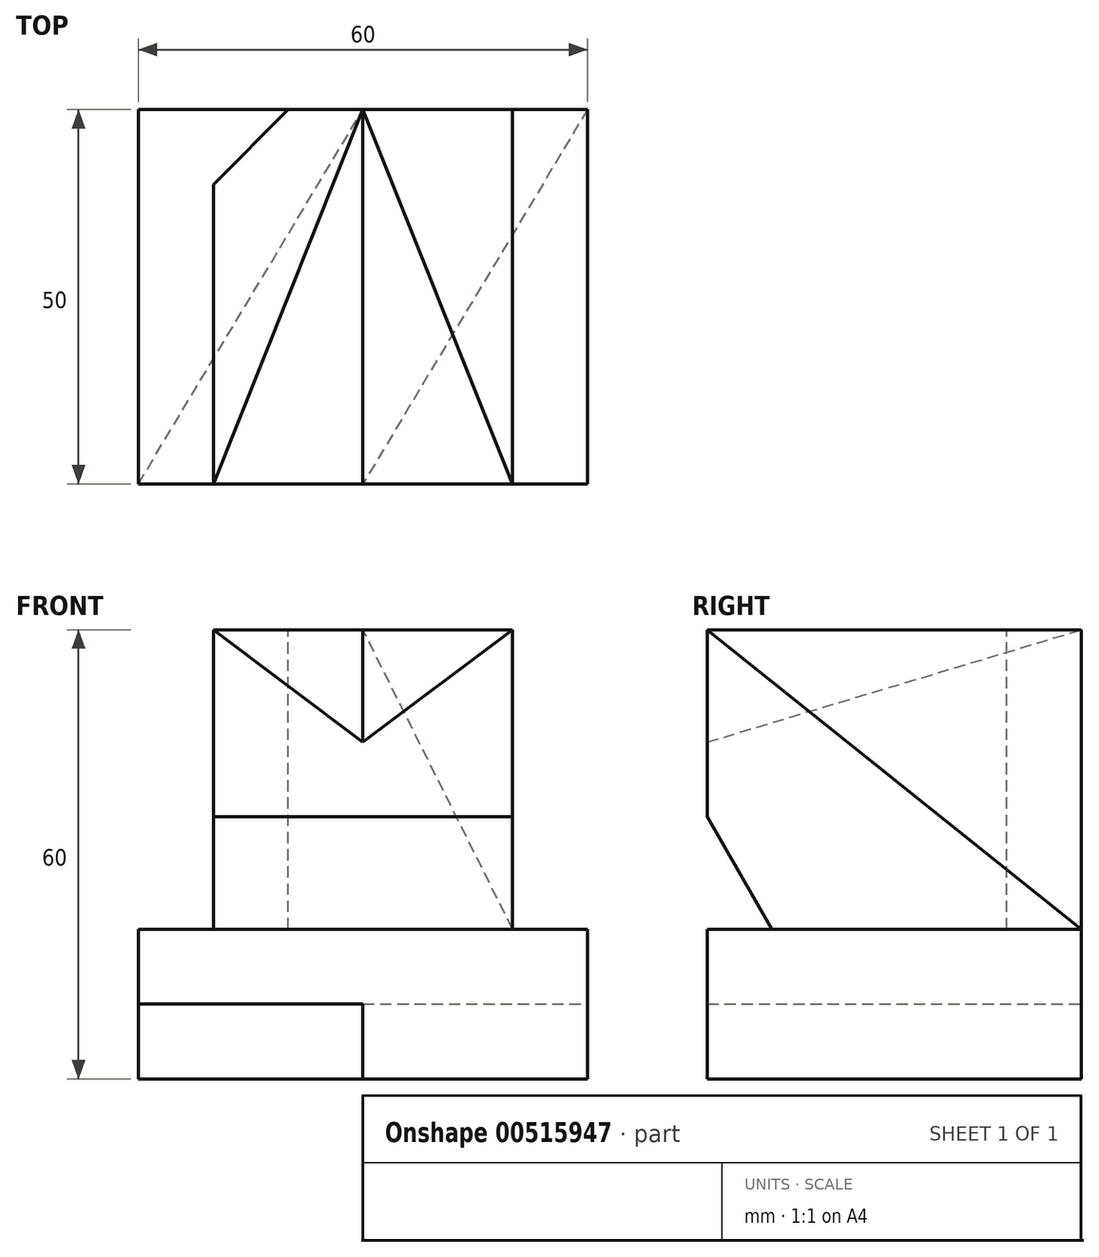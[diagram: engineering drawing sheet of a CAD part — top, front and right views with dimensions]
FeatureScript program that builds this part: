
annotation { "Feature Type Name" : "Feature", "Feature Type Description" : "" }
export const myFeature = defineFeature(function(context is Context, id is Id, definition is map)
    precondition{}
    {
        {
            var Q0;
            Q0=qCreatedBy(makeId("Top.planeOp"),FACE);
            var sketch = newSketch(context, id + "F0", { "sketchPlane" : qUnion([Q0])});
            skLineSegment(sketch, "E0.bottom", {"start": v(0, 0) * mm, "end": v(60, 0) * mm});
            skLineSegment(sketch, "E0.top", {"start": v(0, 50) * mm, "end": v(60, 50) * mm});
            skLineSegment(sketch, "E0.left", {"start": v(0, 0) * mm, "end": v(0, 50) * mm});
            skLineSegment(sketch, "E0.right", {"start": v(60, 0) * mm, "end": v(60, 50) * mm});
            skSolve(sketch);
        }
        {
            var Q0;
            Q0 = qSketchRegion(id + "F0", true);
            extrude(context, id + "F1", {"entities" : qUnion([Q0]), "depth" : 20 * mm, "offsetDistance" : 25 * mm});
        }
        {
            var Q0;
            Q0=makeQuery(id+"F1.opExtrude","CAP_FACE",FACE,{"disambiguationData":[OSD([sQuery(id+"F0.wireOp",EDGE,"E0.bottom"),sQuery(id+"F0.wireOp",EDGE,"E0.top"),sQuery(id+"F0.wireOp",EDGE,"E0.left"),sQuery(id+"F0.wireOp",EDGE,"E0.right")])],"isStart":false});
            var sketch = newSketch(context, id + "F2", { "sketchPlane" : qUnion([Q0])});
            skLineSegment(sketch, "E1.bottom", {"start": v(10, 50) * mm, "end": v(50, 50) * mm});
            skLineSegment(sketch, "E1.top", {"start": v(10, 0) * mm, "end": v(50, 0) * mm});
            skLineSegment(sketch, "E1.left", {"start": v(10, 50) * mm, "end": v(10, 0) * mm});
            skLineSegment(sketch, "E1.right", {"start": v(50, 50) * mm, "end": v(50, 0) * mm});
            skSolve(sketch);
        }
        {
            var Q0;
            Q0 = qSketchRegion(id + "F2", true);
            extrude(context, id + "F3", {"entities" : qUnion([Q0]), "operationType" : NewBodyOperationType.ADD, "depth" : 40 * mm, "offsetDistance" : 25 * mm});
        }
        {
            var Q0;
            Q0=makeQuery(id+"F1.opExtrude","CAP_FACE",FACE,{"disambiguationData":[OSD([sQuery(id+"F0.wireOp",EDGE,"E0.bottom"),sQuery(id+"F0.wireOp",EDGE,"E0.top"),sQuery(id+"F0.wireOp",EDGE,"E0.left"),sQuery(id+"F0.wireOp",EDGE,"E0.right")])],"isStart":true});
            var sketch = newSketch(context, id + "F4", { "sketchPlane" : qUnion([Q0])});
            skLineSegment(sketch, "E2", {"start": v(0, 0) * mm, "end": v(30, -50) * mm});
            skLineSegment(sketch, "E3", {"start": v(60, -50) * mm, "end": v(30, 0) * mm});
            skSolve(sketch);
        }
        {
            var Q0;
            Q0 = qSketchRegion(id + "F4", true);
            var Q1;
            {var subQ0=sQuery(id+"F4.wireOp",EDGE,"E2");Q1=makeQuery(id+"F4.imprint","IMPRINT",FACE,{"disambiguationData":[TD([[makeQuery(id+"F4.imprint","IMPRINT",EDGE,{"derivedFrom":subQ0}),1.0]])]});}
            extrude(context, id + "F5", {"entities" : qUnion([Q0, Q1]), "operationType" : NewBodyOperationType.REMOVE, "oppositeDirection" : true, "depth" : 10 * mm, "offsetDistance" : 25 * mm});
        }
        {
            var Q0;
            Q0=makeQuery(id+"F3.boolean.opBoolean","MERGE",FACE,{"derivedFrom":[makeQuery(id+"F1.opExtrude","SWEPT_FACE",FACE,{"disambiguationData":[OSD([sQuery(id+"F0.wireOp",EDGE,"E0.bottom")])]}),makeQuery(id+"F3.opExtrude","SWEPT_FACE",FACE,{"disambiguationData":[OSD([sQuery(id+"F2.wireOp",EDGE,"E1.top")])]})]});
            var sketch = newSketch(context, id + "F6", { "sketchPlane" : qUnion([Q0])});
            skLineSegment(sketch, "E4", {"start": v(10, 60) * mm, "end": v(30, 45) * mm});
            skLineSegment(sketch, "E5", {"start": v(30, 45) * mm, "end": v(50, 60) * mm});
            skSolve(sketch);
        }
        {
            var Q0;
            Q0=makeQuery(id+"F3.opExtrude","SWEPT_FACE",FACE,{"disambiguationData":[OSD([sQuery(id+"F2.wireOp",EDGE,"E1.right")])]});
            var sketch = newSketch(context, id + "F7", { "sketchPlane" : qUnion([Q0])});
            skLineSegment(sketch, "E6", {"start": v(0, 45) * mm, "end": v(50, 60) * mm});
            skSolve(sketch);
        }
        {
            var Q0;
            Q0=makeQuery(id+"F6.imprint","IMPRINT",FACE,{"disambiguationData":[TD([[makeQuery(id+"F6.imprint","IMPRINT",EDGE,{"derivedFrom":sQuery(id+"F6.wireOp",EDGE,"E4")}),1.0]])]});
            var Q1;
            Q1=sQuery(id+"F7.wireOp",EDGE,"E6");
            sweep(context, id + "F8", {"operationType" : NewBodyOperationType.REMOVE, "profiles" : qUnion([Q0]), "path" : qUnion([Q1])});
        }
        {
            var Q0;
            {var subQ0=sQuery(id+"F2.wireOp",EDGE,"E1.bottom");var subQ2=sQuery(id+"F2.wireOp",EDGE,"E1.left");var subQ3=sQuery(id+"F2.wireOp",EDGE,"E1.top");var subQ4=makeQuery(id+"F3.opExtrude","CAP_FACE",FACE,{"disambiguationData":[OSD([subQ0,subQ3,subQ2,sQuery(id+"F2.wireOp",EDGE,"E1.right")])],"isStart":false});Q0=makeQuery(id+"F8.boolean.opBoolean","SPLIT",FACE,{"disambiguationData":[TD([makeQuery(id+"F3.opExtrude","SWEPT_FACE",FACE,{"disambiguationData":[OSD([subQ2])]})])],"derivedFrom":subQ4});}
            var sketch = newSketch(context, id + "F9", { "sketchPlane" : qUnion([Q0])});
            skLineSegment(sketch, "E7", {"start": v(10, 50) * mm, "end": v(20, 50) * mm});
            skLineSegment(sketch, "E8", {"start": v(10, 50) * mm, "end": v(10, 40) * mm});
            skLineSegment(sketch, "E9", {"start": v(20, 50) * mm, "end": v(10, 40) * mm});
            skSolve(sketch);
        }
        {
            var Q0;
            Q0=makeQuery(id+"F9.imprint","IMPRINT",FACE,{"disambiguationData":[TD([[makeQuery(id+"F9.imprint","IMPRINT",EDGE,{"derivedFrom":sQuery(id+"F9.wireOp",EDGE,"E7")}),-1.0]])]});
            extrude(context, id + "F10", {"entities" : qUnion([Q0]), "operationType" : NewBodyOperationType.REMOVE, "oppositeDirection" : true, "depth" : 40 * mm, "offsetDistance" : 25 * mm});
        }
        {
            var Q0;
            Q0=makeQuery(id+"F3.opExtrude","SWEPT_FACE",FACE,{"disambiguationData":[OSD([sQuery(id+"F2.wireOp",EDGE,"E1.left")])]});
            var sketch = newSketch(context, id + "F11", { "sketchPlane" : qUnion([Q0])});
            skLineSegment(sketch, "E10", {"start": v(0, 35) * mm, "end": v(-8.66, 20) * mm});
            skSolve(sketch);
        }
        {
            var Q0;
            {var subQ0=sQuery(id+"F11.wireOp",EDGE,"E10");Q0=makeQuery(id+"F11.imprint","IMPRINT",FACE,{"disambiguationData":[TD([[makeQuery(id+"F11.imprint","IMPRINT",EDGE,{"derivedFrom":subQ0}),1.0]])]});}
            extrude(context, id + "F12", {"entities" : qUnion([Q0]), "operationType" : NewBodyOperationType.REMOVE, "endBound" : BoundingType.THROUGH_ALL, "oppositeDirection" : true, "depth" : 25 * mm, "offsetDistance" : 25 * mm});
        }
        {
            var Q0;
            Q0=makeQuery(id+"F3.opExtrude","SWEPT_FACE",FACE,{"disambiguationData":[OSD([sQuery(id+"F2.wireOp",EDGE,"E1.right")])]});
            var sketch = newSketch(context, id + "F13", { "sketchPlane" : qUnion([Q0])});
            skLineSegment(sketch, "E11", {"start": v(0, 60) * mm, "end": v(50, 20) * mm});
            skSolve(sketch);
        }
        {
            var Q0;
            Q0=makeQuery(id+"F3.boolean.opBoolean","MERGE",FACE,{"derivedFrom":[makeQuery(id+"F1.opExtrude","SWEPT_FACE",FACE,{"disambiguationData":[OSD([sQuery(id+"F0.wireOp",EDGE,"E0.top")])]}),makeQuery(id+"F3.opExtrude","SWEPT_FACE",FACE,{"disambiguationData":[OSD([sQuery(id+"F2.wireOp",EDGE,"E1.bottom")])]})]});
            var sketch = newSketch(context, id + "F14", { "sketchPlane" : qUnion([Q0])});
            skLineSegment(sketch, "E12", {"start": v(-50, 20) * mm, "end": v(-30, 60) * mm});
            skSolve(sketch);
        }
        {
            var Q0;
            Q0=makeQuery(id+"F13.imprint","IMPRINT",FACE,{"disambiguationData":[TD([[makeQuery(id+"F13.imprint","IMPRINT",EDGE,{"derivedFrom":sQuery(id+"F13.wireOp",EDGE,"E11")}),1.0]])]});
            var Q1;
            Q1=sQuery(id+"F14.wireOp",EDGE,"E12");
            sweep(context, id + "F15", {"operationType" : NewBodyOperationType.REMOVE, "profiles" : qUnion([Q0]), "path" : qUnion([Q1])});
        }
    });
